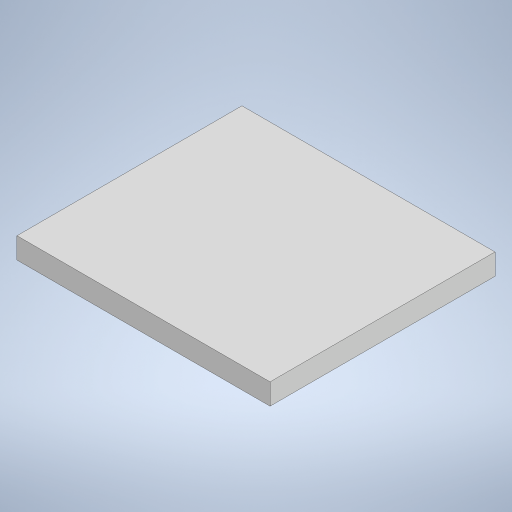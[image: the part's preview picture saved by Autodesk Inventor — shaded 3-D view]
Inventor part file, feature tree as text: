
AUTODESK INVENTOR PART (.ipt)
format: ipt  version: 2024 (Build 280153000, 153)  size: 505,856 bytes
history: native  units: mm
features: other x1, extrude x1
ambient origin geometry x8: Origin, YZ Plane, XZ Plane, XY Plane, X Axis, Y Axis, Z Axis, Center Point
bodies: Body1 (feature_tree)
feature tree (2):
  other  "Sólido1"
  extrude  "Extrusão1"  Depth=18.0mm
